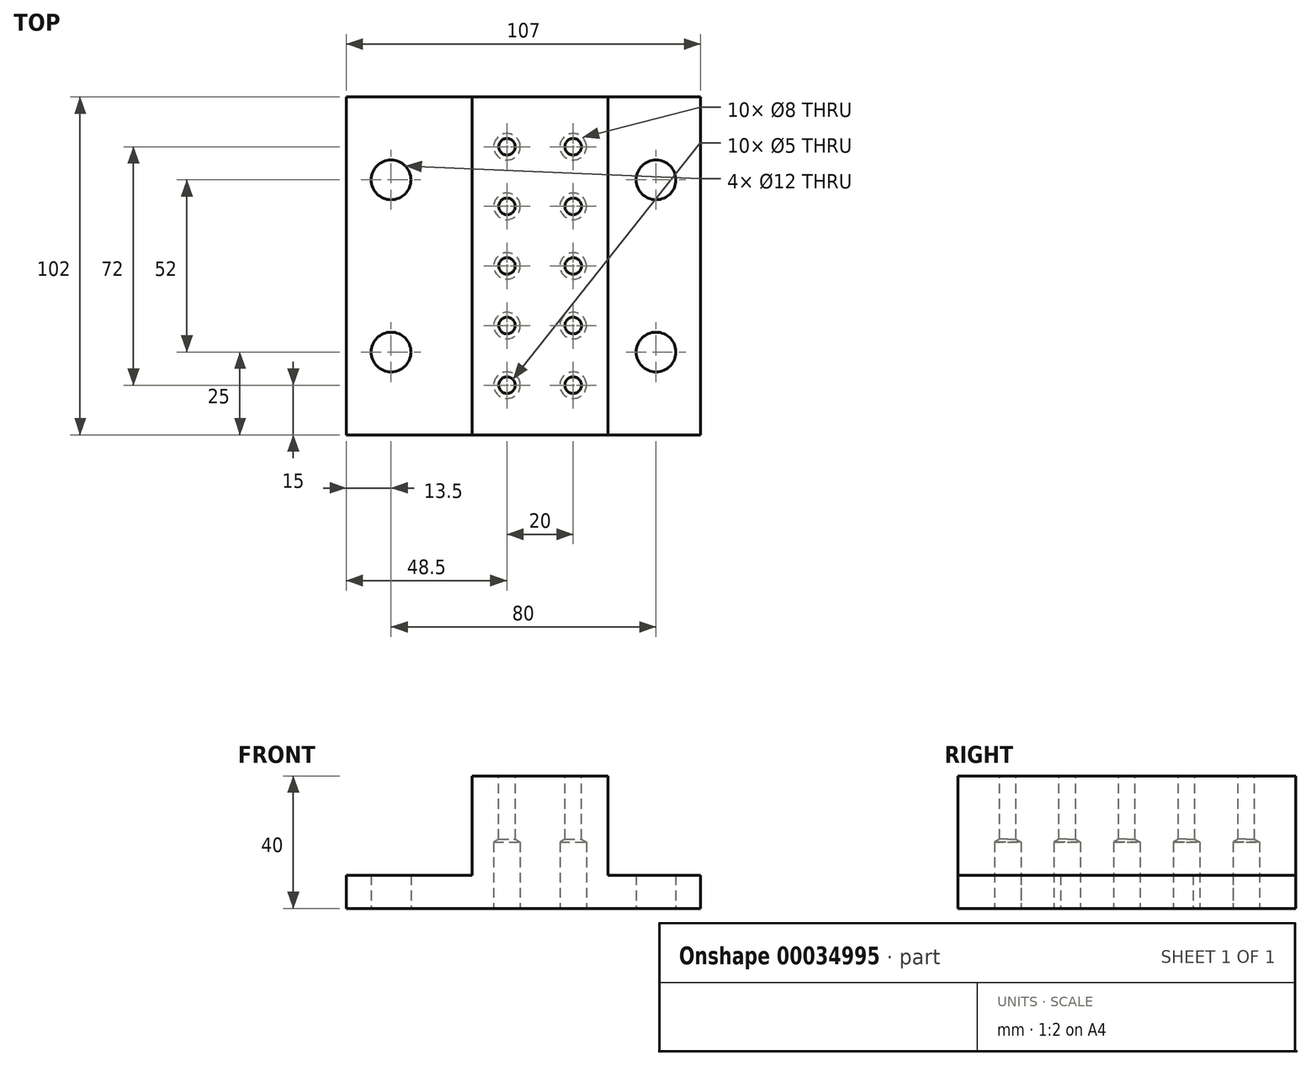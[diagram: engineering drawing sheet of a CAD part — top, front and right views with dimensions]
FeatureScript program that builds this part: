
annotation { "Feature Type Name" : "Feature", "Feature Type Description" : "" }
export const myFeature = defineFeature(function(context is Context, id is Id, definition is map)
    precondition{}
    {
        {
            var Q0;
            Q0=qCreatedBy(makeId("Top.planeOp"),FACE);
            var sketch = newSketch(context, id + "F0", { "sketchPlane" : qUnion([Q0])});
            skLineSegment(sketch, "E0.bottom", {"start": v(-53.5, 51) * mm, "end": v(53.5, 51) * mm});
            skLineSegment(sketch, "E0.top", {"start": v(-53.5, -51) * mm, "end": v(53.5, -51) * mm});
            skLineSegment(sketch, "E0.left", {"start": v(-53.5, 51) * mm, "end": v(-53.5, -51) * mm});
            skLineSegment(sketch, "E0.right", {"start": v(53.5, 51) * mm, "end": v(53.5, -51) * mm});
            skLineSegment(sketch, "E1", {"start": v(0, 51) * mm, "end": v(0, 0) * mm, "construction": true});
            skLineSegment(sketch, "E2", {"start": v(0, 0) * mm, "end": v(53.5, 0) * mm, "construction": true});
            skSolve(sketch);
        }
        {
            var Q0;
            Q0 = qSketchRegion(id + "F0", true);
            extrude(context, id + "F1", {"entities" : qUnion([Q0]), "depth" : 40 * mm});
        }
        {
            var Q0;
            Q0=makeQuery(id+"F1.opExtrude","CAP_FACE",FACE,{"disambiguationData":[OSD([sQuery(id+"F0.wireOp",EDGE,"E0.bottom"),sQuery(id+"F0.wireOp",EDGE,"E0.top"),sQuery(id+"F0.wireOp",EDGE,"E0.left"),sQuery(id+"F0.wireOp",EDGE,"E0.right")])],"isStart":false});
            var sketch = newSketch(context, id + "F2", { "sketchPlane" : qUnion([Q0])});
            skLineSegment(sketch, "E3.bottom", {"start": v(-53.5, 51) * mm, "end": v(-15.5, 51) * mm});
            skLineSegment(sketch, "E3.top", {"start": v(-53.5, -51) * mm, "end": v(-15.5, -51) * mm});
            skLineSegment(sketch, "E3.left", {"start": v(-53.5, 51) * mm, "end": v(-53.5, -51) * mm});
            skLineSegment(sketch, "E3.right", {"start": v(-15.5, 51) * mm, "end": v(-15.5, -51) * mm});
            skLineSegment(sketch, "E4.bottom", {"start": v(53.5, 51) * mm, "end": v(25.5, 51) * mm});
            skLineSegment(sketch, "E4.top", {"start": v(53.5, -51) * mm, "end": v(25.5, -51) * mm});
            skLineSegment(sketch, "E4.left", {"start": v(53.5, 51) * mm, "end": v(53.5, -51) * mm});
            skLineSegment(sketch, "E4.right", {"start": v(25.5, 51) * mm, "end": v(25.5, -51) * mm});
            skLineSegment(sketch, "E5", {"start": v(-15.5, 51) * mm, "end": v(5, 51) * mm, "construction": true});
            skLineSegment(sketch, "E6", {"start": v(5, 51) * mm, "end": v(5, -51) * mm, "construction": true});
            skLineSegment(sketch, "E7", {"start": v(5, -51) * mm, "end": v(25.5, -51) * mm, "construction": true});
            skSolve(sketch);
        }
        {
            var Q0;
            Q0 = qSketchRegion(id + "F2", true);
            extrude(context, id + "F3", {"entities" : qUnion([Q0]), "operationType" : NewBodyOperationType.REMOVE, "oppositeDirection" : true, "depth" : 30 * mm});
        }
        {
            var Q0;
            Q0=makeQuery(id+"F1.opExtrude","CAP_FACE",FACE,{"disambiguationData":[OSD([sQuery(id+"F0.wireOp",EDGE,"E0.bottom"),sQuery(id+"F0.wireOp",EDGE,"E0.top"),sQuery(id+"F0.wireOp",EDGE,"E0.left"),sQuery(id+"F0.wireOp",EDGE,"E0.right")])],"isStart":true});
            var sketch = newSketch(context, id + "F4", { "sketchPlane" : qUnion([Q0])});
            skLineSegment(sketch, "E8.bottom", {"start": v(-5, 36) * mm, "end": v(15, 36) * mm, "construction": true});
            skLineSegment(sketch, "E8.top", {"start": v(-5, -36) * mm, "end": v(15, -36) * mm, "construction": true});
            skLineSegment(sketch, "E8.left", {"start": v(-5, 36) * mm, "end": v(-5, -36) * mm, "construction": true});
            skLineSegment(sketch, "E8.right", {"start": v(15, 36) * mm, "end": v(15, -36) * mm, "construction": true});
            skLineSegment(sketch, "E9", {"start": v(5, 36) * mm, "end": v(5, 51) * mm, "construction": true});
            skLineSegment(sketch, "E10", {"start": v(5, -36) * mm, "end": v(5, -51) * mm, "construction": true});
            skPoint(sketch, "E11", {"position": v(15, 18) * mm});
            skPoint(sketch, "E12", {"position": v(15, 0) * mm});
            skPoint(sketch, "E13", {"position": v(15, -18) * mm});
            skPoint(sketch, "E14", {"position": v(-5, 18) * mm});
            skPoint(sketch, "E15", {"position": v(-5, 0) * mm});
            skPoint(sketch, "E16", {"position": v(-5, -18) * mm});
            skSolve(sketch);
        }
        {
            var Q0;
            Q0=sQuery(id+"F4.wireOp",VERTEX,"E16");
            var Q1;
            Q1=sQuery(id+"F4.wireOp",VERTEX,"E8.left.end");
            var Q2;
            Q2=sQuery(id+"F4.wireOp",VERTEX,"E8.right.end");
            var Q3;
            Q3=sQuery(id+"F4.wireOp",VERTEX,"E13");
            var Q4;
            Q4=sQuery(id+"F4.wireOp",VERTEX,"E15");
            var Q5;
            Q5=sQuery(id+"F4.wireOp",VERTEX,"E12");
            var Q6;
            Q6=sQuery(id+"F4.wireOp",VERTEX,"E11");
            var Q7;
            Q7=sQuery(id+"F4.wireOp",VERTEX,"E14");
            var Q8;
            Q8=sQuery(id+"F4.wireOp",VERTEX,"E8.left.start");
            var Q9;
            Q9=sQuery(id+"F4.wireOp",VERTEX,"E8.right.start");
            var Q10;
            Q10=makeQuery(id+"F1.opExtrude","SWEPT_BODY",BODY,{"disambiguationData":[OSD([sQuery(id+"F0.wireOp",EDGE,"E0.bottom"),sQuery(id+"F0.wireOp",EDGE,"E0.top"),sQuery(id+"F0.wireOp",EDGE,"E0.left"),sQuery(id+"F0.wireOp",EDGE,"E0.right")])]});
            hole(context, id + "F5", {"style" : HoleStyle.SIMPLE, "holeDiameter" : 8 * mm, "endStyle" : HoleEndStyle.BLIND, "holeDepth" : 20 * mm, "locations" : qUnion([Q0, Q1, Q2, Q3, Q4, Q5, Q6, Q7, Q8, Q9]), "scope" : qUnion([Q10])});
        }
        {
            var Q0;
            Q0=makeQuery(id+"F1.opExtrude","CAP_FACE",FACE,{"disambiguationData":[OSD([sQuery(id+"F0.wireOp",EDGE,"E0.bottom"),sQuery(id+"F0.wireOp",EDGE,"E0.top"),sQuery(id+"F0.wireOp",EDGE,"E0.left"),sQuery(id+"F0.wireOp",EDGE,"E0.right")])],"isStart":false});
            var sketch = newSketch(context, id + "F6", { "sketchPlane" : qUnion([Q0])});
            skPoint(sketch, "E17.0", {"position": v(15, -36) * mm});
            skPoint(sketch, "E17.1", {"position": v(-5, -36) * mm});
            skPoint(sketch, "E17.2", {"position": v(-5, -18) * mm});
            skPoint(sketch, "E17.3", {"position": v(15, -18) * mm});
            skPoint(sketch, "E17.4", {"position": v(-5, 0) * mm});
            skPoint(sketch, "E17.5", {"position": v(15, 0) * mm});
            skPoint(sketch, "E17.6", {"position": v(15, 18) * mm});
            skPoint(sketch, "E17.7", {"position": v(-5, 18) * mm});
            skPoint(sketch, "E17.8", {"position": v(-5, 36) * mm});
            skPoint(sketch, "E17.9", {"position": v(15, 36) * mm});
            skSolve(sketch);
        }
        {
            var Q0;
            Q0=sQuery(id+"F6.wireOp",VERTEX,"E17.1");
            var Q1;
            Q1=sQuery(id+"F6.wireOp",VERTEX,"E17.0");
            var Q2;
            Q2=sQuery(id+"F6.wireOp",VERTEX,"E17.2");
            var Q3;
            Q3=sQuery(id+"F6.wireOp",VERTEX,"E17.3");
            var Q4;
            Q4=sQuery(id+"F6.wireOp",VERTEX,"E17.4");
            var Q5;
            Q5=sQuery(id+"F6.wireOp",VERTEX,"E17.5");
            var Q6;
            Q6=sQuery(id+"F6.wireOp",VERTEX,"E17.7");
            var Q7;
            Q7=sQuery(id+"F6.wireOp",VERTEX,"E17.6");
            var Q8;
            Q8=sQuery(id+"F6.wireOp",VERTEX,"E17.8");
            var Q9;
            Q9=sQuery(id+"F6.wireOp",VERTEX,"E17.9");
            var Q10;
            Q10=makeQuery(id+"F1.opExtrude","SWEPT_BODY",BODY,{"disambiguationData":[OSD([sQuery(id+"F0.wireOp",EDGE,"E0.bottom"),sQuery(id+"F0.wireOp",EDGE,"E0.top"),sQuery(id+"F0.wireOp",EDGE,"E0.left"),sQuery(id+"F0.wireOp",EDGE,"E0.right")])]});
            hole(context, id + "F7", {"style" : HoleStyle.SIMPLE, "holeDiameter" : 5 * mm, "endStyle" : HoleEndStyle.THROUGH, "locations" : qUnion([Q0, Q1, Q2, Q3, Q4, Q5, Q6, Q7, Q8, Q9]), "scope" : qUnion([Q10])});
        }
        {
            var Q0;
            Q0=makeQuery(id+"F4.imprint","IMPRINT",FACE,{"disambiguationData":[TD([[makeQuery(id+"F4.imprint","IMPRINT",EDGE,{"derivedFrom":makeQuery(id+"F1.opExtrude","CAP_EDGE",EDGE,{"disambiguationData":[OSD([sQuery(id+"F0.wireOp",EDGE,"E0.bottom")])],"isStart":true})}),1.0]])]});
            var sketch = newSketch(context, id + "F8", { "sketchPlane" : qUnion([Q0])});
            skLineSegment(sketch, "E18.bottom", {"start": v(-40, 26) * mm, "end": v(40, 26) * mm, "construction": true});
            skLineSegment(sketch, "E18.top", {"start": v(-40, -26) * mm, "end": v(40, -26) * mm, "construction": true});
            skLineSegment(sketch, "E18.left", {"start": v(-40, 26) * mm, "end": v(-40, -26) * mm, "construction": true});
            skLineSegment(sketch, "E18.right", {"start": v(40, 26) * mm, "end": v(40, -26) * mm, "construction": true});
            skLineSegment(sketch, "E19", {"start": v(0, 26) * mm, "end": v(0, 0) * mm, "construction": true});
            skLineSegment(sketch, "E20", {"start": v(0, 0) * mm, "end": v(40, 0) * mm, "construction": true});
            skSolve(sketch);
        }
        {
            var Q0;
            Q0=sQuery(id+"F8.wireOp",VERTEX,"E18.left.start");
            var Q1;
            Q1=sQuery(id+"F8.wireOp",VERTEX,"E18.left.end");
            var Q2;
            Q2=sQuery(id+"F8.wireOp",VERTEX,"E18.top.end");
            var Q3;
            Q3=sQuery(id+"F8.wireOp",VERTEX,"E18.right.start");
            var Q4;
            Q4=makeQuery(id+"F1.opExtrude","SWEPT_BODY",BODY,{"disambiguationData":[OSD([sQuery(id+"F0.wireOp",EDGE,"E0.bottom"),sQuery(id+"F0.wireOp",EDGE,"E0.top"),sQuery(id+"F0.wireOp",EDGE,"E0.left"),sQuery(id+"F0.wireOp",EDGE,"E0.right")])]});
            hole(context, id + "F9", {"style" : HoleStyle.SIMPLE, "holeDiameter" : 12 * mm, "endStyle" : HoleEndStyle.THROUGH, "locations" : qUnion([Q0, Q1, Q2, Q3]), "scope" : qUnion([Q4])});
        }
    });
